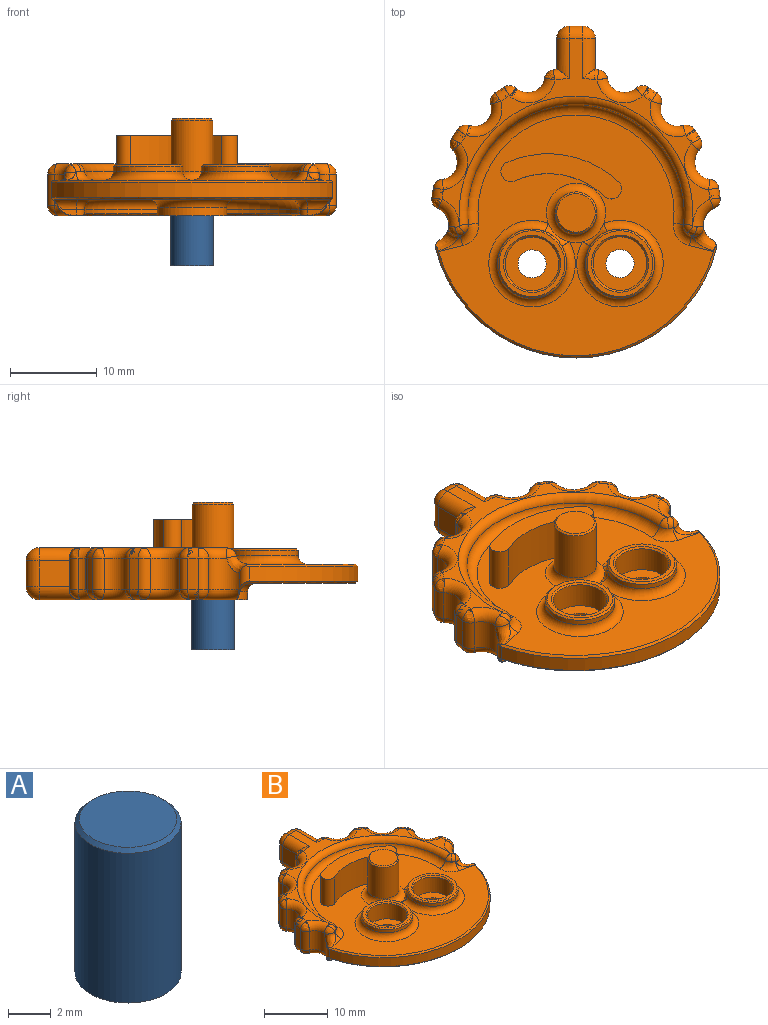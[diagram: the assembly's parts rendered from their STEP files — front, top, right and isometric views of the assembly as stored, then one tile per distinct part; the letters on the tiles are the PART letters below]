
ASSEMBLY  parts=2 mates=1
PART A: 4 faces, bbox 5x5x8.8 mm
  f0: cylinder r=2.48mm len=8.55mm, axis (0,0,-1), area 133mm2, adj f2,f3
  f1: plane 4.55x4.55mm, normal (0,0,1), area 16.3mm2, adj f3
  f2: plane 4.95x4.95mm, normal (0,0,-1), area 19.2mm2, adj f0
  f3: cone r=2.27mm half-angle=45deg, axis (0,0,-1), area 4.2mm2, adj f0,f1
PART B: 180 faces, bbox 33.4x38.4x11.5 mm
  f0: plane 31.77x27.83mm, normal (0,0,-1), area 495.7mm2, adj f1,f168,f169,f170,f171,f172,f173,f174
  f1: cylinder r=1.2mm len=3.09mm, axis (-0.97,0.24,0), area 4.3mm2, adj f0,f2,f168,f172
  f2: plane 2.2x1.21mm, normal (-0.24,-0.97,0), area 1mm2, adj f1,f3,f166,f167,f172
  f3: bspline ~1.85x1.33mm, area 0.3mm2, adj f2,f4,f165,f166
  f4: torus R=3.2mm, axis (0,0,1), area 8.4mm2, adj f3,f5,f163,f164
  f5: sphere r=1.2mm, area 1.8mm2, adj f4,f6,f162
  f6: cylinder r=1.2mm len=3.6mm, axis (0,0,1), area 5.5mm2, adj f5,f7,f161,f164
  f7: cylinder r=16.75mm len=3.6mm, axis (0,0,-1), area 4.3mm2, adj f6,f8,f160,f162
  f8: torus R=15.55mm, axis (0,0,1), area 2.2mm2, adj f7,f9,f159,f161
  f9: plane 30.94x21.71mm, normal (0,0,1), area 51mm2, adj f8,f10,f139,f140,f141,f142,f143,f144
  f10: cylinder r=1.5mm len=1.5mm, axis (1,0,0), area 3.5mm2, adj f9,f11,f137,f138
  f11: plane 3x1.5mm, normal (0,1,0), area 4.5mm2, adj f10,f12,f103,f136
  f12: cylinder r=1.5mm len=3mm, axis (0,0,1), area 7.1mm2, adj f11,f13,f102,f138
  f13: plane 3.5x3mm, normal (-1,0,0), area 10.5mm2, adj f12,f14,f101,f158
  f14: cylinder r=16.75mm len=3.6mm, axis (0,0,-1), area 1.4mm2, adj f13,f15,f100,f101,f157,f158
  f15: cylinder r=1.2mm len=3.6mm, axis (0,0,1), area 5.3mm2, adj f14,f16,f98,f99
  f16: cylinder r=2mm len=3.6mm, axis (0,0,-1), area 15.2mm2, adj f15,f17,f96,f156
  f17: torus R=3.2mm, axis (0,0,1), area 9.7mm2, adj f16,f18,f98,f163
  f18: sphere r=1.2mm, area 1mm2, adj f17,f19,f96
  f19: torus R=15.55mm, axis (0,0,1), area 2.3mm2, adj f18,f20,f95,f163
  f20: cylinder r=16.75mm len=3.6mm, axis (0,0,-1), area 4.5mm2, adj f19,f21,f96,f155
  f21: cylinder r=1.2mm len=3.6mm, axis (0,0,1), area 5.4mm2, adj f20,f22,f23,f95
  f22: sphere r=1.2mm, area 1mm2, adj f21,f154,f155
  f23: cylinder r=2mm len=3.6mm, axis (0,0,-1), area 15.5mm2, adj f21,f24,f93,f154
  f24: torus R=3.2mm, axis (0,0,1), area 9.9mm2, adj f23,f25,f95,f163
  f25: sphere r=1.2mm, area 1mm2, adj f24,f26,f93
  f26: torus R=15.55mm, axis (0,0,1), area 2.2mm2, adj f25,f27,f92,f163
  f27: cylinder r=16.75mm len=3.6mm, axis (0,0,-1), area 4.4mm2, adj f26,f28,f93,f153
  f28: cylinder r=1.2mm len=3.6mm, axis (0,0,1), area 5.5mm2, adj f27,f29,f30,f92
  f29: sphere r=1.2mm, area 1mm2, adj f28,f152,f153
  f30: cylinder r=2mm len=3.6mm, axis (0,0,-1), area 15.7mm2, adj f28,f31,f90,f152
  f31: torus R=3.2mm, axis (0,0,1), area 10mm2, adj f30,f32,f92,f163
  f32: sphere r=1.2mm, area 1mm2, adj f31,f33,f90
  f33: torus R=15.55mm, axis (0,0,1), area 2.2mm2, adj f32,f34,f89,f163
  f34: cylinder r=16.75mm len=3.6mm, axis (0,0,-1), area 4.3mm2, adj f33,f35,f90,f151
  f35: cylinder r=1.2mm len=3.6mm, axis (0,0,1), area 5.5mm2, adj f34,f36,f37,f89
  f36: sphere r=1.2mm, area 1mm2, adj f35,f150,f151
  f37: cylinder r=2mm len=3.6mm, axis (0,0,-1), area 13.7mm2, adj f35,f38,f47,f48,f88,f150,f172
  f38: torus R=3.2mm, axis (0,0,1), area 8.4mm2, adj f37,f39,f89,f163
  f39: bspline ~1.85x1.33mm, area 0.3mm2, adj f38,f40,f46,f47
  f40: plane 2.2x1.21mm, normal (0.24,-0.97,0), area 1mm2, adj f39,f41,f46,f171,f172
  f41: cylinder r=1.2mm len=1.29mm, axis (0,0,-1), area 1mm2, adj f40,f42,f43,f45,f170
  f42: cylinder r=12.53mm len=25.05mm, axis (0,0,-1), area 18.9mm2, adj f41,f43,f167,f169
  f43: cone r=12.78mm half-angle=45deg, axis (0,0,-1), area 15.3mm2, adj f41,f42,f44,f45,f163,f167
  f44: cone r=1.13mm half-angle=45deg, axis (0,0,1), area 0.1mm2, adj f43,f163,f166,f167
  f45: cone r=1.13mm half-angle=45deg, axis (0,0,1), area 0.1mm2, adj f41,f43,f46,f163
  f46: plane 0.39x0.16mm, normal (0.17,-0.69,-0.71), area 0mm2, adj f39,f40,f45,f163
  f47: plane 0.13x0.06mm, normal (-0.91,-0.41,0), area 0mm2, adj f37,f39,f172
  f48: cylinder r=1mm len=2.52mm, axis (0,0,1), area 2.5mm2, adj f37,f49,f87,f88,f172
  f49: cone r=16.5mm half-angle=45deg, axis (0,0,-1), area 15.6mm2, adj f48,f50,f83,f84,f85,f86,f87,f88
  f50: plane 31.77x27.83mm, normal (0,0,1), area 367mm2, adj f49,f51,f52,f55,f58,f60,f61,f62
  f51: torus R=11.33mm, axis (0,0,1), area 69.5mm2, adj f50,f52,f55,f148
  f52: torus R=2.4mm, axis (0,0,1), area 4.1mm2, adj f50,f51,f53,f83,f147
  f53: bspline ~1.46x1.08mm, area 1.3mm2, adj f52,f54,f146,f147
  f54: bspline ~1.38x1.21mm, area 1.6mm2, adj f53,f83,f84,f146
  f55: torus R=2.4mm, axis (0,0,1), area 4.1mm2, adj f50,f51,f56,f86,f149
  f56: bspline ~1.43x1.05mm, area 1mm2, adj f55,f57,f149,f150
  f57: bspline ~1.51x1.36mm, area 1.6mm2, adj f56,f86,f88,f150
  f58: cylinder r=9.47mm len=10.55mm, axis (0,0,-1), area 58.6mm2, adj f50,f59,f60,f62
  f59: plane 13.91x5.22mm, normal (0,0,1), area 32.9mm2, adj f58,f60,f61,f62
  f60: cylinder r=1.16mm len=5.15mm, axis (0,0,-1), area 17mm2, adj f50,f58,f59,f61
  f61: cylinder r=11.77mm len=13.11mm, axis (0,0,-1), area 72.9mm2, adj f50,f59,f60,f62
  f62: cylinder r=1.16mm len=5.15mm, axis (0,0,-1), area 17.4mm2, adj f50,f58,f59,f61
  f63: torus R=5mm, axis (0,0,1), area 38.5mm2, adj f50,f64,f65
  f64: bspline ~2.82x2.62mm, area 3mm2, adj f63,f65,f79
  f65: cylinder r=4mm len=8mm, axis (0,0,-1), area 15.1mm2, adj f63,f64,f66
  f66: cone r=3.8mm half-angle=45deg, axis (0,0,-1), area 6.9mm2, adj f65,f67
  f67: plane 7.6x7.6mm, normal (0,0,1), area 11.2mm2, adj f66,f68
  f68: cone r=3.3mm half-angle=45deg, axis (0,0,1), area 5.7mm2, adj f67,f69
  f69: cylinder r=3.1mm len=6.2mm, axis (0,0,-1), area 57.5mm2, adj f68,f70
  f70: plane 6.2x6.2mm, normal (0,0,1), area 21.9mm2, adj f69,f173
  f71: torus R=5mm, axis (0,0,1), area 38.5mm2, adj f50,f72,f73
  f72: bspline ~2.82x2.62mm, area 3mm2, adj f71,f73,f79
  f73: cylinder r=4mm len=8mm, axis (0,0,-1), area 15.1mm2, adj f71,f72,f74
  f74: cone r=4mm half-angle=45deg, axis (0,0,-1), area 6.9mm2, adj f73,f75
  f75: plane 7.6x7.6mm, normal (0,0,1), area 11.2mm2, adj f74,f76
  f76: cone r=3.3mm half-angle=45deg, axis (0,0,1), area 5.7mm2, adj f75,f77
  f77: cylinder r=3.1mm len=6.2mm, axis (0,0,-1), area 57.5mm2, adj f76,f78
  f78: plane 6.2x6.2mm, normal (0,0,1), area 21.9mm2, adj f77,f174
  f79: torus R=3.43mm, axis (0,0,1), area 27.5mm2, adj f50,f64,f72,f80
  f80: cylinder r=2.43mm len=5.95mm, axis (0,0,-1), area 90.7mm2, adj f79,f81
  f81: cone r=2.23mm half-angle=45deg, axis (0,0,-1), area 4.1mm2, adj f80,f82
  f82: plane 4.45x4.45mm, normal (0,0,1), area 15.6mm2, adj f81
  f83: cylinder r=1.2mm len=3.09mm, axis (0.97,-0.24,0), area 1.4mm2, adj f49,f50,f52,f54,f84
  f84: bspline ~2.96x2.86mm, area 5.1mm2, adj f49,f54,f83,f85,f164
  f85: cylinder r=1mm len=2.52mm, axis (0,0,1), area 2.5mm2, adj f49,f84,f87,f164,f172
  f86: cylinder r=1.2mm len=3.09mm, axis (0.97,0.24,0), area 1.4mm2, adj f49,f50,f55,f57,f88
  f87: cylinder r=16.75mm len=32.41mm, axis (0,0,-1), area 74.9mm2, adj f48,f49,f85,f172
  f88: bspline ~2.96x2.86mm, area 5.1mm2, adj f37,f48,f49,f57,f86
  f89: sphere r=1.2mm, area 2.7mm2, adj f33,f35,f38
  f90: cylinder r=1.2mm len=3.6mm, axis (0,0,1), area 5.5mm2, adj f30,f32,f34,f91
  f91: sphere r=1.2mm, area 2.7mm2, adj f90,f151,f152
  f92: sphere r=1.2mm, area 2.6mm2, adj f26,f28,f31
  f93: cylinder r=1.2mm len=3.6mm, axis (0,0,1), area 5.4mm2, adj f23,f25,f27,f94
  f94: sphere r=1.2mm, area 3.3mm2, adj f93,f153,f154
  f95: sphere r=1.2mm, area 2.6mm2, adj f19,f21,f24
  f96: cylinder r=1.2mm len=3.6mm, axis (0,0,1), area 5.3mm2, adj f16,f18,f20,f97
  f97: sphere r=1.2mm, area 3mm2, adj f96,f155,f156
  f98: sphere r=1.2mm, area 2.6mm2, adj f15,f17,f100
  f99: sphere r=1.2mm, area 1mm2, adj f15,f156,f157
  f100: torus R=15.55mm, axis (0,0,1), area 2mm2, adj f14,f98,f101,f163
  f101: cylinder r=1.5mm len=4.57mm, axis (0,-1,0), area 9mm2, adj f13,f14,f100,f102,f163
  f102: sphere r=1.5mm, area 2.2mm2, adj f12,f101,f103
  f103: cylinder r=1.5mm len=1.5mm, axis (-1,0,0), area 3.5mm2, adj f11,f102,f104,f163
  f104: sphere r=1.5mm, area 2.3mm2, adj f103,f105,f136
  f105: cylinder r=1.5mm len=4.57mm, axis (0,1,0), area 9mm2, adj f104,f106,f134,f135,f163
  f106: cylinder r=16.75mm len=3.6mm, axis (0,0,-1), area 1.4mm2, adj f105,f107,f134,f135,f139,f140
  f107: cylinder r=1.2mm len=3.6mm, axis (0,0,1), area 5.3mm2, adj f106,f108,f132,f133
  f108: cylinder r=2mm len=3.6mm, axis (0,0,-1), area 15.2mm2, adj f107,f109,f130,f141
  f109: cylinder r=1.2mm len=3.6mm, axis (0,0,1), area 5.3mm2, adj f108,f110,f128,f129
  f110: cylinder r=16.75mm len=3.6mm, axis (0,0,-1), area 4.5mm2, adj f109,f111,f126,f142
  f111: torus R=15.55mm, axis (0,0,1), area 2.3mm2, adj f110,f112,f129,f163
  f112: sphere r=1.2mm, area 1.3mm2, adj f111,f113,f126
  f113: torus R=3.2mm, axis (0,0,1), area 9.9mm2, adj f112,f114,f125,f163
  f114: sphere r=1.2mm, area 1.8mm2, adj f113,f115,f123
  f115: torus R=15.55mm, axis (0,0,1), area 2.2mm2, adj f114,f116,f122,f163
  f116: sphere r=1.2mm, area 1.5mm2, adj f115,f117,f120
  f117: torus R=3.2mm, axis (0,0,1), area 10mm2, adj f116,f118,f119,f163
  f118: sphere r=1.2mm, area 1.8mm2, adj f117,f160,f162
  f119: cylinder r=2mm len=3.6mm, axis (0,0,-1), area 15.7mm2, adj f117,f120,f145,f160
  f120: cylinder r=1.2mm len=3.6mm, axis (0,0,1), area 5.5mm2, adj f116,f119,f121,f122
  f121: sphere r=1.2mm, area 2.7mm2, adj f120,f144,f145
  f122: cylinder r=16.75mm len=3.6mm, axis (0,0,-1), area 4.4mm2, adj f115,f120,f123,f144
  f123: cylinder r=1.2mm len=3.6mm, axis (0,0,1), area 5.4mm2, adj f114,f122,f124,f125
  f124: sphere r=1.2mm, area 1.3mm2, adj f123,f143,f144
  f125: cylinder r=2mm len=3.6mm, axis (0,0,-1), area 15.5mm2, adj f113,f123,f126,f143
  f126: cylinder r=1.2mm len=3.6mm, axis (0,0,1), area 5.4mm2, adj f110,f112,f125,f127
  f127: sphere r=1.2mm, area 2.6mm2, adj f126,f142,f143
  f128: sphere r=1.2mm, area 1.5mm2, adj f109,f141,f142
  f129: sphere r=1.2mm, area 1.8mm2, adj f109,f111,f130
  f130: torus R=3.2mm, axis (0,0,1), area 9.7mm2, adj f108,f129,f131,f133,f163
  f131: sphere r=1.2mm, area 0.3mm2, adj f130,f135
  f132: sphere r=1.2mm, area 2.7mm2, adj f107,f140,f141
  f133: sphere r=1.2mm, area 0.6mm2, adj f107,f130,f135
  f134: plane 3.5x3mm, normal (1,0,0), area 10.5mm2, adj f105,f106,f136,f139
  f135: torus R=15.55mm, axis (0,0,1), area 2mm2, adj f105,f106,f131,f133,f163
  f136: cylinder r=1.5mm len=3mm, axis (0,0,-1), area 7.1mm2, adj f11,f104,f134,f137
  f137: sphere r=1.5mm, area 2.3mm2, adj f10,f136,f139
  f138: sphere r=1.5mm, area 4.8mm2, adj f10,f12,f158
  f139: cylinder r=1.5mm len=4.57mm, axis (0,-1,0), area 9mm2, adj f9,f106,f134,f137,f140
  f140: torus R=15.55mm, axis (0,0,1), area 2mm2, adj f9,f106,f132,f139
  f141: torus R=3.2mm, axis (0,0,1), area 9.7mm2, adj f9,f108,f128,f132
  f142: torus R=15.55mm, axis (0,0,1), area 2.3mm2, adj f9,f110,f127,f128
  f143: torus R=3.2mm, axis (0,0,1), area 9.9mm2, adj f9,f124,f125,f127
  f144: torus R=15.55mm, axis (0,0,1), area 2.2mm2, adj f9,f121,f122,f124
  f145: torus R=3.2mm, axis (0,0,1), area 10mm2, adj f9,f119,f121,f159
  f146: torus R=3.2mm, axis (0,0,1), area 5.9mm2, adj f9,f53,f54,f161,f164
  f147: torus R=0.22mm, axis (0,0,-1), area 1.1mm2, adj f9,f52,f53,f148
  f148: torus R=13.51mm, axis (0,0,1), area 62mm2, adj f9,f51,f147,f149
  f149: torus R=0.22mm, axis (0,0,-1), area 1.1mm2, adj f9,f55,f56,f148
  f150: torus R=3.2mm, axis (0,0,1), area 5.9mm2, adj f9,f36,f37,f56,f57
  f151: torus R=15.55mm, axis (0,0,1), area 2.2mm2, adj f9,f34,f36,f91
  f152: torus R=3.2mm, axis (0,0,1), area 10mm2, adj f9,f29,f30,f91
  f153: torus R=15.55mm, axis (0,0,1), area 2.2mm2, adj f9,f27,f29,f94
  f154: torus R=3.2mm, axis (0,0,1), area 9.9mm2, adj f9,f22,f23,f94
  f155: torus R=15.55mm, axis (0,0,1), area 2.3mm2, adj f9,f20,f22,f97
  f156: torus R=3.2mm, axis (0,0,1), area 9.7mm2, adj f9,f16,f97,f99
  f157: torus R=15.55mm, axis (0,0,1), area 2mm2, adj f9,f14,f99,f158
  f158: cylinder r=1.5mm len=4.57mm, axis (0,1,0), area 9mm2, adj f9,f13,f14,f138,f157
  f159: sphere r=1.2mm, area 1.9mm2, adj f8,f145,f160
  f160: cylinder r=1.2mm len=3.6mm, axis (0,0,1), area 5.5mm2, adj f7,f118,f119,f159
  f161: sphere r=1.2mm, area 2.7mm2, adj f6,f8,f146
  f162: torus R=15.55mm, axis (0,0,1), area 2.2mm2, adj f5,f7,f118,f163
  f163: plane 30.94x22.73mm, normal (0,0,-1), area 84.9mm2, adj f4,f17,f19,f24,f26,f31,f33,f38
  f164: cylinder r=2mm len=3.6mm, axis (0,0,-1), area 13.7mm2, adj f4,f6,f84,f85,f146,f165,f172
  f165: bspline ~0.13x0.06mm, area 0mm2, adj f3,f164,f172
  f166: plane 0.39x0.16mm, normal (-0.17,-0.69,-0.71), area 0mm2, adj f2,f3,f44,f163
  f167: cylinder r=1.2mm len=1.29mm, axis (0,0,-1), area 1mm2, adj f2,f42,f43,f44,f168
  f168: torus R=2.4mm, axis (0,0,1), area 4.4mm2, adj f0,f1,f167,f169
  f169: torus R=11.33mm, axis (0,0,1), area 76.4mm2, adj f0,f42,f168,f170
  f170: torus R=2.4mm, axis (0,0,1), area 4.4mm2, adj f0,f41,f169,f171
  f171: cylinder r=1.2mm len=3.09mm, axis (-0.97,-0.24,0), area 4.3mm2, adj f0,f40,f170,f172
  f172: cone r=16.75mm half-angle=45deg, axis (0,0,1), area 16.7mm2, adj f0,f1,f2,f37,f40,f47,f48,f85
  f173: cylinder r=1.62mm len=3.25mm, axis (0,0,-1), area 8.7mm2, adj f0,f70
  f174: cylinder r=1.62mm len=3.25mm, axis (0,0,-1), area 8.7mm2, adj f0,f78
  f175: torus R=5mm, axis (0,0,1), area 43.1mm2, adj f0,f176
  f176: cylinder r=4mm len=8mm, axis (0,0,1), area 22.6mm2, adj f175,f177
  f177: plane 8x8mm, normal (0,0,-1), area 31.8mm2, adj f176,f178
  f178: cylinder r=2.43mm len=4.85mm, axis (0,0,-1), area 45.7mm2, adj f177,f179
  f179: plane 4.85x4.85mm, normal (0,0,-1), area 18.5mm2, adj f178
PLACE A t=(7.39,-7.94,-8.17)mm
PLACE B t=(7.39,-7.94,0.61)mm
MATE slider A.f0 <-> B.f79  axis (0,0,-1) through (7.39,-7.94,-8.17)mm
